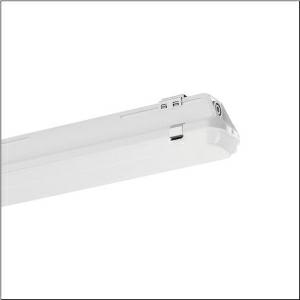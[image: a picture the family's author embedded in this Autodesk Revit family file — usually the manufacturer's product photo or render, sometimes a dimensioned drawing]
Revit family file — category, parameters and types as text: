
# Revit family: monsun_r__21_51fb107p460c_c7f7
name_source: partatom
category: Lighting Fixtures
units: mm (PartAtom-declared; Revit-internal decimal feet)

## family parameters
Cut with Voids When Loaded = No
Host = Face
Light Source = No
Part Type = Normal
Room Calculation Point = No
Round Connector Dimension = Use Diameter
Shared = No

## types (1)
- Monsun® 21 (1 x LED, 6200 lm, 34.9 W, 4000K)
    Apparent Load = 35 VA
    CIE Flux Codes = 47 77 93 94 100
    Color Rendering = 80
    Color Temperature = 4000K
    Default Elevation = 1800 mm
    Description = Monsun® 21, damp-proof luminaire, chain hanger, primary optical cover: enclosure, of PMMA, light emission: direct distribution, primary light characteristic: symmetric, installation type: suspended mounting, surface-mounted, horizontal mounting, vertical mounting, LED, rated luminous flux: 6.200lm, luminous efficacy: 178lm/W, light colour: 840, colour temperature: 4000K, control gear: ON/OFF, with terminal, 3-pole, max. 2.5mm², mains connection: 220..240V, AC, 50/60Hz, rated input power: 35W, housing, of glass-fibre reinforced polyester, uncoated, bright grey, incl. chain hanger, length: 1.590mm, width: 90mm, height: 88mm, clip for enclosure, of stainless steel (V2A), ceiling mounting element, of stainless steel (V2A), chain hanger, of stainless steel (V2A), protection rating (complete): IP66, insulation class (complete): insulation class I (protective earthing), certification: CE, ENEC, VDE, UKCA, protection symbol: D, impact resistance: IK04, permissible operating ambient temperature: -25..+35°C, standard: EN 50419, EN 60598-2-1, corresponds to IFS (International Featured Standards) requirements for safety and quality in the food industry, for indoor or canopied outdoor use, no direct snow, no direct sun, no direct rain, LABS conformity tested according to VDMA 24364:2018-05, contact your sales advisor before using the luminaires in applications with unclear chemical exposure, large temperature fluctuations or condensation-forming humidity, packaging unit: 1 piece
    Height = 89 mm
    Lamp = 1 x LED
    Lamp Light Flux = 6200 lm
    Lamp Power = 34.9 W
    Lamp count = 1
    Length = 1590 mm
    Luminous efficacy = 178 lm/W
    Manufacturer = Siteco
    ModVariant = No
    Model = 51FB107P460C
    Mounting Place = Ceiling
    Mounting Type = Surface mounted
    Number of Poles = 1
    OnlyDefault = Yes
    Power Factor = 1
    Product Name = Monsun® 21
    Product group = damp-proof luminaire
    ProductGroupID = 300
    Protection Class = Protection class I
    Protection Degree = IP 66
    RLX_Detail_Level = 1
    RLX_Emergency_Light_Flux = 0 lm
    RLX_Emergency_Type = 0
    RLX_Emergency_Type_DB = No
    RlxData = <blob elided: 88425 chars, md5=5df45326>
    Socket = socket
    Standby Power = 0 W
    System Light Flux = 6200 lm
    System Power = 35 W
    Type Comments = Product without accessories
    Type Image = l_1319656.jpg
    URL = http://relux.com
    VarID = ---
    Voltage = 0 V
    Weight = 0.00 kg
    Width = 90 mm

## geometry (parser evidence)
native form markers: Blend x4, Sweep x14
no freeform markers — native parametric forms only
